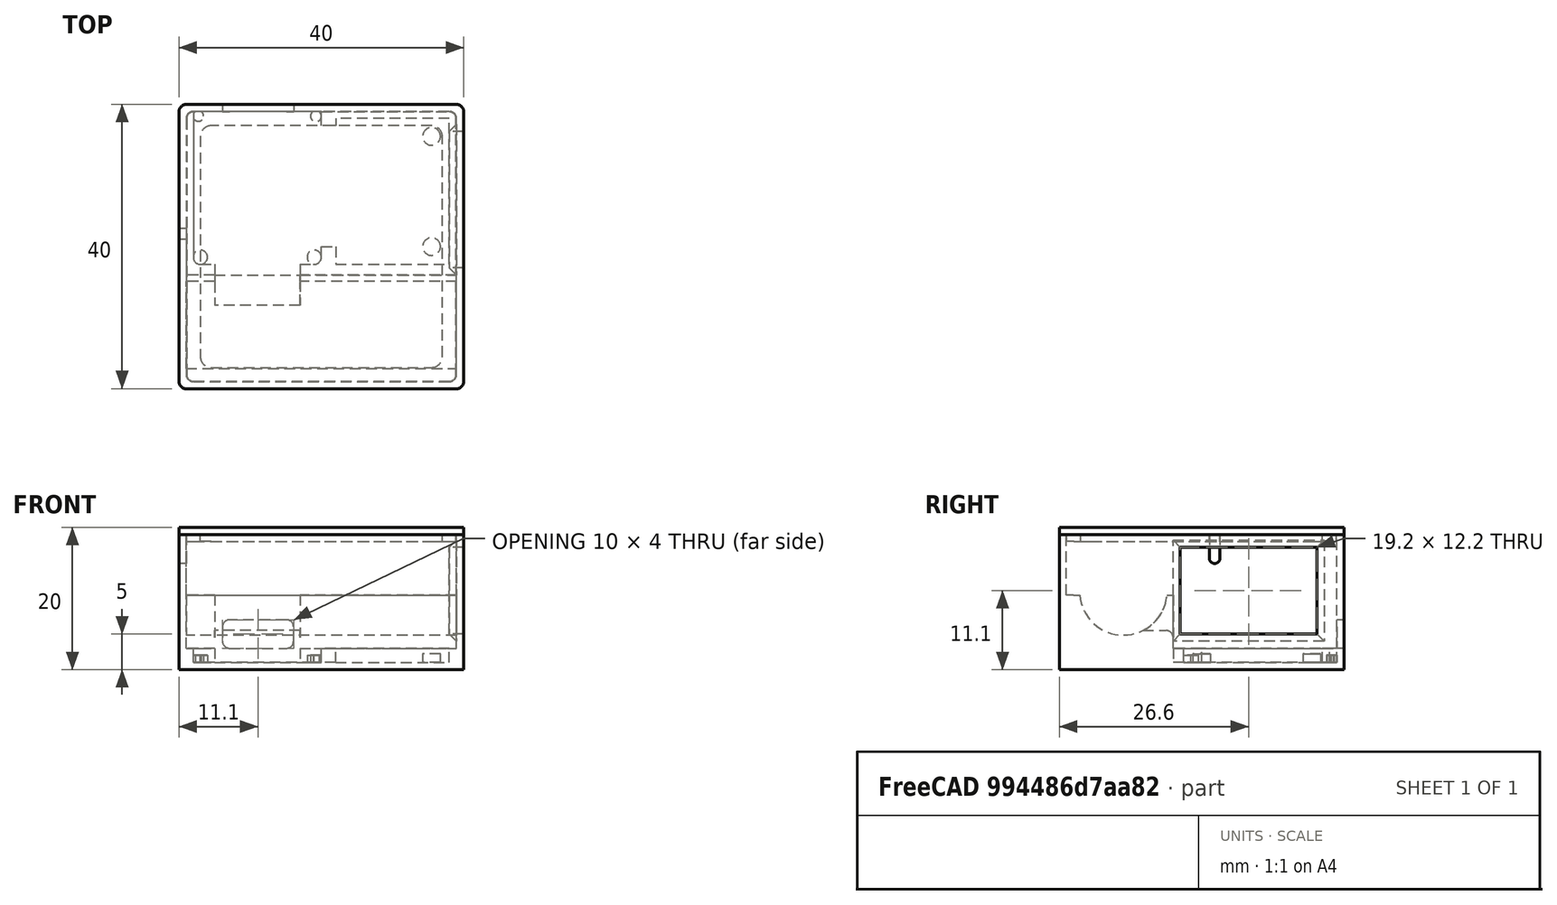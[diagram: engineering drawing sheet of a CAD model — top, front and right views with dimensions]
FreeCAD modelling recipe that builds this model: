
FCSTD DOCUMENT  (FreeCAD 1.0R39319 (Git))
Label: box
License: All rights reserved
LicenseURL: https://en.wikipedia.org/wiki/All_rights_reserved
objects: Sketcher::SketchObject×14, PartDesign::Pad×12, PartDesign::Pocket×6, PartDesign::Chamfer×2, PartDesign::Body×2, Mesh::Feature×2, PartDesign::Plane×1, PartDesign::Fillet×1
note: 94 computed .brp shape members not serialized (recipe doc carries the construction recipe); baked Part::Feature solids carry a one-line shape summary decoded from their .brp

FEATURE [Sketcher::SketchObject] Sketch
  ArcFitTolerance = 1e-06
  AttachmentSupport = -> [XY_Plane]
  FullyConstrained = true
  MakeInternals = false
  MapMode = 5
  sketch-geometry (12):
    g0: LineSegment StartX=1 StartY=0 StartZ=0 EndX=39 EndY=0 EndZ=0
    g1: LineSegment StartX=40 StartY=1 StartZ=0 EndX=40 EndY=39 EndZ=0
    g2: LineSegment StartX=39 StartY=40 StartZ=0 EndX=1 EndY=40 EndZ=0
    g3: LineSegment StartX=0 StartY=39 StartZ=0 EndX=0 EndY=1 EndZ=0
    g4: ArcOfCircle CenterX=1 CenterY=39 CenterZ=0 NormalX=0 NormalY=0 NormalZ=1 AngleXU=0 Radius=1 StartAngle=1.5708 EndAngle=3.14159
    g5: GeomPoint [constr] X=0 Y=40 Z=0
    g6: ArcOfCircle CenterX=1 CenterY=1 CenterZ=0 NormalX=0 NormalY=0 NormalZ=1 AngleXU=0 Radius=1 StartAngle=3.14159 EndAngle=4.71239
    g7: GeomPoint [constr] X=0 Y=0 Z=0
    g8: ArcOfCircle CenterX=39 CenterY=1 CenterZ=0 NormalX=0 NormalY=0 NormalZ=1 AngleXU=0 Radius=1 StartAngle=4.71239 EndAngle=6.28319
    g9: GeomPoint [constr] X=40 Y=0 Z=0
    g10: ArcOfCircle CenterX=39 CenterY=39 CenterZ=0 NormalX=0 NormalY=0 NormalZ=1 AngleXU=0 Radius=1 StartAngle=-2.7e-15 EndAngle=1.5708
    g11: GeomPoint [constr] X=40 Y=40 Z=0
  constraints (27):
    c: Horizontal(g0)
    c: Horizontal(g2)
    c: Vertical(g1)
    c: Vertical(g3)
    c: Distance(g9,g7) = 40
    c: Distance(g7,g5) = 40
    c: Coincident(g7,g-1)
    c: PointOnObject(g5,g3)
    c: PointOnObject(g5,g2)
    c: Tangent(g3,g4) = -1.5708
    c: Tangent(g2,g4) = -1.5708
    c: PointOnObject(g7,g0)
    c: PointOnObject(g7,g3)
    c: Tangent(g0,g6) = -1.5708
    c: Tangent(g3,g6) = -1.5708
    c: PointOnObject(g9,g0)
    c: PointOnObject(g9,g1)
    c: Tangent(g0,g8) = -1.5708
    c: Tangent(g1,g8) = -1.5708
    c: PointOnObject(g11,g2)
    c: PointOnObject(g11,g1)
    c: Tangent(g2,g10) = -1.5708
    c: Tangent(g1,g10) = -1.5708
    c: Radius(g10) = 1
    c: Radius(g4) = 1
    c: Radius(g6) = 1
    c: Radius(g8) = 1
FEATURE [PartDesign::Pad] Pad
  Direction = (0,0,1)
  Length = 1
  Length2 = 10
  Profile = -> Sketch
  ReferenceAxis = -> Sketch [N_Axis]
  Refine = true
  Suppressed = false
  Type = 0
FEATURE [Sketcher::SketchObject] Sketch001
  ArcFitTolerance = 1e-06
  AttachmentSupport = -> [Pad]
  FullyConstrained = true
  MakeInternals = false
  MapMode = 5
  Placement = pos=(0,0,1) rot=(0,0,1;0rad)
  sketch-geometry (24):
    g0: LineSegment StartX=1 StartY=0 StartZ=0 EndX=39 EndY=0 EndZ=0
    g1: LineSegment StartX=40 StartY=1 StartZ=0 EndX=40 EndY=39 EndZ=0
    g2: LineSegment StartX=39 StartY=40 StartZ=0 EndX=1 EndY=40 EndZ=0
    g3: LineSegment StartX=0 StartY=39 StartZ=0 EndX=0 EndY=1 EndZ=0
    g4: ArcOfCircle CenterX=1 CenterY=39 CenterZ=0 NormalX=0 NormalY=0 NormalZ=1 AngleXU=0 Radius=1 StartAngle=1.5708 EndAngle=3.14159
    g5: GeomPoint [constr] X=0 Y=40 Z=0
    g6: ArcOfCircle CenterX=1 CenterY=1 CenterZ=0 NormalX=0 NormalY=0 NormalZ=1 AngleXU=0 Radius=1 StartAngle=3.14159 EndAngle=4.71239
    g7: GeomPoint [constr] X=0 Y=0 Z=0
    g8: ArcOfCircle CenterX=39 CenterY=1 CenterZ=0 NormalX=0 NormalY=0 NormalZ=1 AngleXU=0 Radius=1 StartAngle=4.71239 EndAngle=6.28319
    g9: GeomPoint [constr] X=40 Y=0 Z=0
    g10: ArcOfCircle CenterX=39 CenterY=39 CenterZ=0 NormalX=0 NormalY=0 NormalZ=1 AngleXU=0 Radius=1 StartAngle=-1.8e-15 EndAngle=1.5708
    g11: GeomPoint [constr] X=40 Y=40 Z=0
    g12: LineSegment StartX=2 StartY=1 StartZ=0 EndX=38 EndY=1 EndZ=0
    g13: LineSegment StartX=39 StartY=2 StartZ=0 EndX=39 EndY=38 EndZ=0
    g14: LineSegment StartX=38 StartY=39 StartZ=0 EndX=2 EndY=39 EndZ=0
    g15: LineSegment StartX=1 StartY=38 StartZ=0 EndX=1 EndY=2 EndZ=0
    g16: ArcOfCircle CenterX=2 CenterY=38 CenterZ=0 NormalX=0 NormalY=0 NormalZ=1 AngleXU=0 Radius=1 StartAngle=1.5708 EndAngle=3.14159
    g17: GeomPoint [constr] X=1 Y=39 Z=0
    g18: ArcOfCircle CenterX=38 CenterY=38 CenterZ=0 NormalX=0 NormalY=0 NormalZ=1 AngleXU=0 Radius=1 StartAngle=1.6e-15 EndAngle=1.5708
    g19: GeomPoint [constr] X=39 Y=39 Z=0
    g20: ArcOfCircle CenterX=38 CenterY=2 CenterZ=0 NormalX=0 NormalY=0 NormalZ=1 AngleXU=0 Radius=1 StartAngle=4.71239 EndAngle=6.28319
    g21: GeomPoint [constr] X=39 Y=1 Z=0
    g22: ArcOfCircle CenterX=2 CenterY=2 CenterZ=0 NormalX=0 NormalY=0 NormalZ=1 AngleXU=0 Radius=1 StartAngle=3.14159 EndAngle=4.71239
    g23: GeomPoint [constr] X=1 Y=1 Z=0
  constraints (53):
    c: Horizontal(g0)
    c: Horizontal(g2)
    c: Vertical(g1)
    c: Vertical(g3)
    c: Distance(g9,g7) = 40
    c: Distance(g7,g5) = 40
    c: Coincident(g7,g-1)
    c: PointOnObject(g5,g3)
    c: PointOnObject(g5,g2)
    c: Tangent(g3,g4) = -1.5708
    c: Tangent(g2,g4) = -1.5708
    c: PointOnObject(g7,g0)
    c: PointOnObject(g7,g3)
    c: Tangent(g0,g6) = -1.5708
    c: Tangent(g3,g6) = -1.5708
    c: PointOnObject(g9,g0)
    c: PointOnObject(g9,g1)
    c: Tangent(g0,g8) = -1.5708
    c: Tangent(g1,g8) = -1.5708
    c: PointOnObject(g11,g2)
    c: PointOnObject(g11,g1)
    c: Tangent(g2,g10) = -1.5708
    c: Tangent(g1,g10) = -1.5708
    c: Radius(g10) = 1
    c: Radius(g4) = 1
    c: Radius(g6) = 1
    c: Radius(g8) = 1
    c: Horizontal(g12)
    c: Horizontal(g14)
    c: Vertical(g13)
    c: Vertical(g15)
    c: Coincident(g23,g6)
    c: Coincident(g19,g10)
    c: PointOnObject(g17,g15)
    c: PointOnObject(g17,g14)
    c: Tangent(g15,g16) = -1.5708
    c: Tangent(g14,g16) = -1.5708
    c: PointOnObject(g19,g13)
    c: PointOnObject(g19,g14)
    c: Tangent(g13,g18) = -1.5708
    c: Tangent(g14,g18) = -1.5708
    c: PointOnObject(g21,g13)
    c: PointOnObject(g21,g12)
    c: Tangent(g13,g20) = -1.5708
    c: Tangent(g12,g20) = -1.5708
    c: PointOnObject(g23,g12)
    c: PointOnObject(g23,g15)
    c: Tangent(g12,g22) = -1.5708
    c: Tangent(g15,g22) = -1.5708
    c: Radius(g22) = 1
    c: Radius(g20) = 1
    c: Radius(g18) = 1
    c: Radius(g16) = 1
FEATURE [PartDesign::Pad] Pad001
  BaseFeature = -> Pad
  Direction = (0,0,1)
  Length = 18
  Length2 = 10
  Profile = -> Sketch001
  ReferenceAxis = -> Sketch001 [N_Axis]
  Refine = true
  Suppressed = false
  Type = 0
FEATURE [Sketcher::SketchObject] Sketch002
  ArcFitTolerance = 1e-06
  AttachmentSupport = -> [Pad001]
  FullyConstrained = true
  MakeInternals = false
  MapMode = 5
  Placement = pos=(40,0,0) rot=(0.57735,0.57735,0.57735;2.0944rad)
  sketch-geometry (4):
    g0: LineSegment StartX=36.2 StartY=17.2 StartZ=0 EndX=17 EndY=17.2 EndZ=0
    g1: LineSegment StartX=17 StartY=17.2 StartZ=0 EndX=17 EndY=5 EndZ=0
    g2: LineSegment StartX=17 StartY=5 StartZ=0 EndX=36.2 EndY=5 EndZ=0
    g3: LineSegment StartX=36.2 StartY=5 StartZ=0 EndX=36.2 EndY=17.2 EndZ=0
  constraints (12):
    c: Coincident(g0,g1)
    c: Coincident(g1,g2)
    c: Coincident(g2,g3)
    c: Coincident(g3,g0)
    c: Horizontal(g0)
    c: Horizontal(g2)
    c: Vertical(g1)
    c: Vertical(g3)
    c: Distance(g1,g3) = 19.2
    c: Distance(g0,g2) = 12.2
    c: DistanceY(g-1,g2) = 5
    c: DistanceX(g-1,g0) = 17
FEATURE [PartDesign::Pocket] Pocket
  BaseFeature = -> Pad001
  Direction = (-1,0,0)
  Length = 5
  Length2 = 5
  Profile = -> Sketch002
  ReferenceAxis = -> Sketch002 [N_Axis]
  Refine = true
  Suppressed = false
  Type = 0
FEATURE [Sketcher::SketchObject] Sketch003
  ArcFitTolerance = 1e-06
  AttachmentSupport = -> [Pocket]
  ExternalGeometry = -> [Pocket]
  FullyConstrained = true
  MakeInternals = false
  MapMode = 5
  Placement = pos=(39,0,0) rot=(0.57735,-0.57735,-0.57735;2.0944rad)
  sketch-geometry (8):
    g0: LineSegment StartX=-36.2 StartY=17.2 StartZ=0 EndX=-36.2 EndY=5 EndZ=0
    g1: LineSegment StartX=-36.2 StartY=5 StartZ=0 EndX=-17 EndY=5 EndZ=0
    g2: LineSegment StartX=-17 StartY=5 StartZ=0 EndX=-17 EndY=17.2 EndZ=0
    g3: LineSegment StartX=-17 StartY=17.2 StartZ=0 EndX=-36.2 EndY=17.2 EndZ=0
    g4: LineSegment StartX=-37.2 StartY=18.2 StartZ=0 EndX=-37.2 EndY=4 EndZ=0
    g5: LineSegment StartX=-37.2 StartY=4 StartZ=0 EndX=-16 EndY=4 EndZ=0
    g6: LineSegment StartX=-16 StartY=4 StartZ=0 EndX=-16 EndY=18.2 EndZ=0
    g7: LineSegment StartX=-16 StartY=18.2 StartZ=0 EndX=-37.2 EndY=18.2 EndZ=0
  constraints (22):
    c: Coincident(g0,g1)
    c: Coincident(g1,g2)
    c: Coincident(g2,g3)
    c: Coincident(g3,g0)
    c: Vertical(g0)
    c: Vertical(g2)
    c: Horizontal(g1)
    c: Horizontal(g3)
    c: Coincident(g0,g-3)
    c: Coincident(g1,g-4)
    c: Coincident(g4,g5)
    c: Coincident(g5,g6)
    c: Coincident(g6,g7)
    c: Coincident(g7,g4)
    c: Vertical(g4)
    c: Vertical(g6)
    c: Horizontal(g5)
    c: Horizontal(g7)
    c: DistanceY(g2,g6) = 1
    c: DistanceY(g5,g1) = 1
    c: DistanceX(g1,g5) = 1
    c: DistanceX(g4,g0) = 1
FEATURE [PartDesign::Pad] Pad002
  BaseFeature = -> Pocket
  Direction = (-1,0,0)
  Length = 1
  Length2 = 10
  Profile = -> Sketch003
  ReferenceAxis = -> Sketch003 [N_Axis]
  Refine = true
  Suppressed = false
  Type = 0
FEATURE [PartDesign::Chamfer] Chamfer
  Angle = 45
  Base = -> Pad002 [Edge64,Edge63,Edge61,Edge59]
  BaseFeature = -> Pad002
  ChamferType = 0
  FlipDirection = false
  Refine = true
  Size = 0.99
  Size2 = 1
  SupportTransform = false
  Suppressed = false
  UseAllEdges = false
FEATURE [Sketcher::SketchObject] Sketch004
  ArcFitTolerance = 1e-06
  AttachmentSupport = -> [Chamfer]
  FullyConstrained = false
  MakeInternals = false
  MapMode = 5
  Placement = pos=(0,0,1) rot=(0,0,1;0rad)
  sketch-geometry (24):
    g0: LineSegment StartX=2 StartY=39 StartZ=0 EndX=2 EndY=18.5 EndZ=0
    g1: LineSegment StartX=3 StartY=17.5 StartZ=0 EndX=5 EndY=17.5 EndZ=0
    g2: LineSegment StartX=20 StartY=18.5 StartZ=0 EndX=20 EndY=20 EndZ=0
    g3: ArcOfCircle CenterX=3 CenterY=18.5 CenterZ=0 NormalX=0 NormalY=0 NormalZ=1 AngleXU=0 Radius=1 StartAngle=3.14159 EndAngle=4.71239
    g4: GeomPoint [constr] X=2 Y=17.5 Z=0
    g5: ArcOfCircle CenterX=19 CenterY=18.5 CenterZ=0 NormalX=0 NormalY=0 NormalZ=1 AngleXU=0 Radius=1 StartAngle=4.71239 EndAngle=6.28319
    g6: GeomPoint [constr] X=20 Y=17.5 Z=0
    g7: LineSegment StartX=22 StartY=38 StartZ=0 EndX=22 EndY=37 EndZ=0
    g8: LineSegment StartX=22 StartY=17.5 StartZ=0 EndX=38 EndY=17.5 EndZ=0
    g9: LineSegment StartX=38 StartY=17.5 StartZ=0 EndX=38 EndY=38 EndZ=0
    g10: LineSegment StartX=38 StartY=38 StartZ=0 EndX=22 EndY=38 EndZ=0
    g11: LineSegment StartX=20 StartY=20 StartZ=0 EndX=22 EndY=20 EndZ=0
    g12: LineSegment StartX=22 StartY=37 StartZ=0 EndX=20 EndY=37 EndZ=0
    g13: LineSegment StartX=5 StartY=17.5 StartZ=0 EndX=5 EndY=14 EndZ=0
    g14: LineSegment StartX=17 StartY=17.5 StartZ=0 EndX=17 EndY=14 EndZ=0
    g15: LineSegment StartX=5 StartY=14 StartZ=0 EndX=17 EndY=14 EndZ=0
    g16: LineSegment StartX=17 StartY=17.5 StartZ=0 EndX=19 EndY=17.5 EndZ=0
    g17: LineSegment StartX=20 StartY=37 StartZ=0 EndX=20 EndY=39 EndZ=0
    g18: LineSegment StartX=22 StartY=20 StartZ=0 EndX=22 EndY=17.5 EndZ=0
    g19: LineSegment StartX=1 StartY=1 StartZ=0 EndX=39 EndY=1 EndZ=0
    g20: LineSegment StartX=39 StartY=1 StartZ=0 EndX=39 EndY=39 EndZ=0
    g21: LineSegment StartX=1 StartY=39 StartZ=0 EndX=1 EndY=1 EndZ=0
    g22: LineSegment StartX=1 StartY=39 StartZ=0 EndX=2 EndY=39 EndZ=0
    g23: LineSegment StartX=20 StartY=39 StartZ=0 EndX=39 EndY=39 EndZ=0
  constraints (63):
    c: Vertical(g0)
    c: Vertical(g2)
    c: Horizontal(g1)
    c: Distance(g0,g17) = 18
    c: Distance(g4,g0) = 21.5
    c: PointOnObject(g4,g1)
    c: PointOnObject(g4,g0)
    c: Tangent(g1,g3) = -1.5708
    c: Tangent(g0,g3) = -1.5708
    c: PointOnObject(g6,g16)
    c: PointOnObject(g6,g2)
    c: Coincident(g16,g5) = -1.5708
    c: Tangent(g2,g5) = -1.5708
    c: Coincident(g18,g8)
    c: Coincident(g8,g9)
    c: Coincident(g9,g10)
    c: Coincident(g10,g7)
    c: Vertical(g7)
    c: Vertical(g9)
    c: Horizontal(g8)
    c: Horizontal(g10)
    c: DistanceX(g10,g10) = 16
    c: DistanceY(g9,g9) = 20.5
    c: DistanceX(g-1,g9) = 38
    c: DistanceY(g-1,g7) = 38
    c: PointOnObject(g11,g18)
    c: Horizontal(g11)
    c: PointOnObject(g12,g17)
    c: Horizontal(g12)
    c: DistanceY(g-1,g11) = 20
    c: DistanceY(g-1,g12) = 37
    c: Radius(g3) = 1
    c: Radius(g5) = 1
    c: Vertical(g13)
    c: PointOnObject(g14,g16)
    c: Vertical(g14)
    c: Coincident(g15,g13)
    c: Coincident(g15,g14)
    c: Horizontal(g15)
    c: DistanceY(g13,g13) = 3.5
    c: DistanceX(g-1,g13) = 5
    c: DistanceX(g-1,g14) = 17
    c: Coincident(g1,g13)
    c: PointOnObject(g16,g14)
    c: Coincident(g2,g11)
    c: PointOnObject(g17,g12)
    c: Coincident(g7,g12)
    c: PointOnObject(g18,g11)
    c: Coincident(g19,g20)
    c: Coincident(g21,g19)
    c: Horizontal(g19)
    c: Vertical(g20)
    c: Vertical(g21)
    c: Distance(g20,g21) = 38
    c: Distance(g19,g21) = 38
    c: DistanceX(g-1,g19) = 1
    c: DistanceY(g-1,g19) = 1
    c: Coincident(g22,g21)
    c: Coincident(g22,g0)
    c: Horizontal(g22)
    c: Coincident(g23,g17)
    c: Coincident(g23,g20)
    c: Horizontal(g23)
FEATURE [PartDesign::Pad] Pad003
  BaseFeature = -> Chamfer
  Direction = (0,0,1)
  Length = 2
  Length2 = 10
  Profile = -> Sketch004
  ReferenceAxis = -> Sketch004 [N_Axis]
  Refine = true
  Suppressed = false
  Type = 0
FEATURE [PartDesign::Chamfer] Chamfer001
  Angle = 45
  Base = -> Pad003 [Edge33]
  BaseFeature = -> Pad003
  ChamferType = 0
  FlipDirection = false
  Refine = true
  Size = 1.8
  Size2 = 1
  SupportTransform = false
  Suppressed = false
  UseAllEdges = false
FEATURE [Sketcher::SketchObject] Sketch005
  ArcFitTolerance = 1e-06
  AttachmentSupport = -> [Chamfer001]
  ExternalGeometry = -> [Chamfer001]
  FullyConstrained = true
  MakeInternals = false
  MapMode = 5
  Placement = pos=(0,0,3) rot=(0,0,1;0rad)
  sketch-geometry (4):
    g0: LineSegment StartX=2 StartY=1 StartZ=0 EndX=38 EndY=1 EndZ=0
    g1: LineSegment StartX=38 StartY=1 StartZ=0 EndX=38 EndY=16 EndZ=0
    g2: LineSegment StartX=38 StartY=16 StartZ=0 EndX=2 EndY=16 EndZ=0
    g3: LineSegment StartX=2 StartY=16 StartZ=0 EndX=2 EndY=1 EndZ=0
  constraints (11):
    c: Coincident(g0,g1)
    c: Coincident(g1,g2)
    c: Coincident(g2,g3)
    c: Coincident(g3,g0)
    c: Horizontal(g0)
    c: Horizontal(g2)
    c: Vertical(g1)
    c: Vertical(g3)
    c: Distance(g1,g3) = 36
    c: Distance(g0,g2) = 15
    c: Coincident(g0,g-3)
FEATURE [PartDesign::Pad] Pad004
  BaseFeature = -> Chamfer001
  Direction = (0,0,1)
  Length = 5
  Length2 = 10
  Midplane = true
  Profile = -> Sketch005
  ReferenceAxis = -> Sketch005 [N_Axis]
  Refine = true
  Suppressed = false
  Type = 0
FEATURE [PartDesign::Pad] Pad005
  BaseFeature = -> Pad004
  Direction = (0,0,1)
  Length = 10
  Length2 = 10
  Profile = -> Pad004 [Face29]
  Refine = true
  Suppressed = false
  Type = 0
FEATURE [Sketcher::SketchObject] Sketch006
  ArcFitTolerance = 1e-06
  AttachmentSupport = -> [Pad005]
  ExternalGeometry = -> [Pad005]
  FullyConstrained = false
  MakeInternals = false
  MapMode = 5
  Placement = pos=(0,0,1) rot=(0,0,1;0rad)
  sketch-geometry (4):
    g0: Circle CenterX=3 CenterY=18.5 CenterZ=0 NormalX=0 NormalY=0 NormalZ=1 AngleXU=0 Radius=1
    g1: Circle CenterX=19 CenterY=18.5 CenterZ=0 NormalX=0 NormalY=0 NormalZ=1 AngleXU=0 Radius=1
    g2: Circle CenterX=2.69921 CenterY=38.3735 CenterZ=0 NormalX=0 NormalY=0 NormalZ=1 AngleXU=0 Radius=0.751416
    g3: Circle CenterX=19.2468 CenterY=38.3457 CenterZ=0 NormalX=0 NormalY=0 NormalZ=1 AngleXU=0 Radius=0.769216
  constraints (4):
    c: Coincident(g0,g-3)
    c: PointOnObject(g-3,g0)
    c: Coincident(g1,g-4)
    c: PointOnObject(g-4,g1)
FEATURE [PartDesign::Pad] Pad006
  BaseFeature = -> Pad005
  Direction = (0,0,1)
  Length = 1
  Length2 = 10
  Profile = -> Sketch006
  ReferenceAxis = -> Sketch006 [N_Axis]
  Refine = true
  Suppressed = false
  Type = 0
FEATURE [Sketcher::SketchObject] Sketch007
  ArcFitTolerance = 1e-06
  AttachmentSupport = -> [Pad006]
  ExternalGeometry = -> [Pad006]
  FullyConstrained = true
  MakeInternals = false
  MapMode = 5
  Placement = pos=(0,0,1) rot=(0,0,1;0rad)
  sketch-geometry (2):
    g0: Circle CenterX=35.5 CenterY=35.5 CenterZ=0 NormalX=0 NormalY=0 NormalZ=1 AngleXU=0 Radius=1.25
    g1: Circle CenterX=35.5 CenterY=20 CenterZ=0 NormalX=0 NormalY=0 NormalZ=1 AngleXU=0 Radius=1.25
  constraints (6):
    c: Diameter(g0) = 2.5
    c: Diameter(g1) = 2.5
    c: DistanceX(g1,g-3) = 2.5
    c: DistanceX(g0,g-3) = 2.5
    c: DistanceY(g0,g-3) = 2.5
    c: DistanceY(g-4,g1) = 2.5
FEATURE [PartDesign::Pad] Pad007
  BaseFeature = -> Pad006
  Direction = (0,0,1)
  Length = 1.2
  Length2 = 10
  Profile = -> Sketch007
  ReferenceAxis = -> Sketch007 [N_Axis]
  Refine = true
  Suppressed = false
  Type = 0
FEATURE [PartDesign::Plane] DatumPlane
  AttachmentOffset = pos=(0,0,20) rot=(0,0,1;0rad)
  AttachmentSupport = -> [YZ_Plane]
  Length = 76.4018
  MapMode = 5
  Placement = pos=(20,0,0) rot=(0.57735,0.57735,0.57735;2.0944rad)
  ResizeMode = 0
  Width = 61.4018
FEATURE [Sketcher::SketchObject] Sketch008
  ArcFitTolerance = 1e-06
  AttachmentSupport = -> [DatumPlane]
  FullyConstrained = true
  MakeInternals = false
  MapMode = 5
  Placement = pos=(20,0,0) rot=(0.57735,0.57735,0.57735;2.0944rad)
  sketch-geometry (1):
    g0: Circle CenterX=9 CenterY=11 CenterZ=0 NormalX=0 NormalY=0 NormalZ=1 AngleXU=0 Radius=6.15
  constraints (3):
    c: Diameter(g0) = 12.3
    c: DistanceY(g-1,g0) = 11
    c: DistanceX(g-1,g0) = 9
FEATURE [PartDesign::Pocket] Pocket001
  BaseFeature = -> Pad007
  Direction = (0,0,-1)
  Length = 5
  Length2 = 5
  Profile = -> Pad007 [Face39]
  Refine = true
  Suppressed = false
  Type = 0
FEATURE [PartDesign::Pocket] Pocket002
  BaseFeature = -> Pocket001
  Direction = (-1,0,0)
  Length = 38
  Length2 = 5
  Midplane = true
  Profile = -> Sketch008
  ReferenceAxis = -> Sketch008 [N_Axis]
  Refine = true
  Suppressed = false
  Type = 0
FEATURE [PartDesign::Pad] Pad008
  BaseFeature = -> Pocket002
  Direction = (-1,0,0)
  Length = 1
  Length2 = 10
  Profile = -> Pocket002 [Face46]
  Refine = true
  Suppressed = false
  Type = 0
FEATURE [PartDesign::Pad] Pad009
  BaseFeature = -> Pad008
  Direction = (1,0,0)
  Length = 1
  Length2 = 10
  Profile = -> Pad008 [Face32]
  Refine = true
  Suppressed = false
  Type = 0
FEATURE [Sketcher::SketchObject] Sketch009
  ArcFitTolerance = 1e-06
  AttachmentSupport = -> [Pad009]
  ExternalGeometry = -> [Pad009]
  FullyConstrained = true
  MakeInternals = false
  MapMode = 5
  Placement = pos=(0,0,10.5) rot=(0,0,1;0rad)
  sketch-geometry (4):
    g0: LineSegment StartX=5 StartY=16 StartZ=0 EndX=5 EndY=11 EndZ=0
    g1: LineSegment StartX=5 StartY=11 StartZ=0 EndX=17 EndY=11 EndZ=0
    g2: LineSegment StartX=17 StartY=11 StartZ=0 EndX=17 EndY=16 EndZ=0
    g3: LineSegment StartX=17 StartY=16 StartZ=0 EndX=5 EndY=16 EndZ=0
  constraints (12):
    c: Coincident(g0,g1)
    c: Coincident(g1,g2)
    c: Coincident(g2,g3)
    c: Coincident(g3,g0)
    c: Vertical(g0)
    c: Vertical(g2)
    c: Horizontal(g1)
    c: Horizontal(g3)
    c: Distance(g0,g2) = 12
    c: Distance(g1,g3) = 5
    c: PointOnObject(g0,g-3)
    c: DistanceX(g-1,g0) = 5
FEATURE [PartDesign::Pocket] Pocket003
  BaseFeature = -> Pad009
  Direction = (0,0,-1)
  Length = 5
  Length2 = 5
  Profile = -> Sketch009
  ReferenceAxis = -> Sketch009 [N_Axis]
  Refine = true
  Suppressed = false
  Type = 0
FEATURE [PartDesign::Fillet] Fillet
  Base = -> Pocket003 [Edge81]
  BaseFeature = -> Pocket003
  Radius = 1
  Refine = true
  SupportTransform = false
  Suppressed = false
  UseAllEdges = false
FEATURE [Sketcher::SketchObject] Sketch010
  ArcFitTolerance = 1e-06
  AttachmentSupport = -> [Fillet]
  FullyConstrained = false
  MakeInternals = false
  MapMode = 5
  Placement = pos=(0,0,0) rot=(0.57735,-0.57735,-0.57735;2.0944rad)
  sketch-geometry (4):
    g0: ArcOfCircle CenterX=-21.8272 CenterY=15.6733 CenterZ=0 NormalX=0 NormalY=0 NormalZ=1 AngleXU=0 Radius=0.75 StartAngle=3.14159 EndAngle=6.28319
    g1: ArcOfCircle CenterX=-21.8272 CenterY=20.6733 CenterZ=0 NormalX=0 NormalY=0 NormalZ=1 AngleXU=0 Radius=0.75 StartAngle=0 EndAngle=3.14159
    g2: LineSegment StartX=-22.5772 StartY=15.6733 StartZ=0 EndX=-22.5772 EndY=20.6733 EndZ=0
    g3: LineSegment StartX=-21.0772 StartY=15.6733 StartZ=0 EndX=-21.0772 EndY=20.6733 EndZ=0
  constraints (8):
    c: Tangent(g0,g2) = 1.5708
    c: Tangent(g0,g3) = -1.5708
    c: Tangent(g1,g2) = 1.5708
    c: Tangent(g1,g3) = -1.5708
    c: Equal(g0,g1)
    c: Vertical(g3)
    c: Distance(g0,g1) = 5
    c: Radius(g0) = 0.75
FEATURE [PartDesign::Pocket] Pocket004
  BaseFeature = -> Fillet
  Direction = (1,0,0)
  Length = 5
  Length2 = 5
  Profile = -> Sketch010
  ReferenceAxis = -> Sketch010 [N_Axis]
  Refine = true
  Suppressed = false
  Type = 0
FEATURE [Sketcher::SketchObject] Sketch011
  ArcFitTolerance = 1e-06
  AttachmentSupport = -> [XY_Plane001]
  FullyConstrained = true
  MakeInternals = false
  MapMode = 5
  sketch-geometry (24):
    g0: LineSegment StartX=2.05 StartY=1.05 StartZ=0 EndX=37.95 EndY=1.05 EndZ=0
    g1: LineSegment StartX=38.95 StartY=2.05 StartZ=0 EndX=38.95 EndY=37.95 EndZ=0
    g2: LineSegment StartX=37.95 StartY=38.95 StartZ=0 EndX=2.05 EndY=38.95 EndZ=0
    g3: LineSegment StartX=1.05 StartY=37.95 StartZ=0 EndX=1.05 EndY=2.05 EndZ=0
    g4: ArcOfCircle CenterX=2.05 CenterY=2.05 CenterZ=0 NormalX=0 NormalY=0 NormalZ=1 AngleXU=0 Radius=1 StartAngle=3.14159 EndAngle=4.71239
    g5: GeomPoint [constr] X=1.05 Y=1.05 Z=0
    g6: ArcOfCircle CenterX=37.95 CenterY=2.05 CenterZ=0 NormalX=0 NormalY=0 NormalZ=1 AngleXU=0 Radius=1 StartAngle=4.71239 EndAngle=6.28319
    g7: GeomPoint [constr] X=38.95 Y=1.05 Z=0
    g8: ArcOfCircle CenterX=2.05 CenterY=37.95 CenterZ=0 NormalX=0 NormalY=0 NormalZ=1 AngleXU=0 Radius=1 StartAngle=1.5708 EndAngle=3.14159
    g9: GeomPoint [constr] X=1.05 Y=38.95 Z=0
    g10: ArcOfCircle CenterX=37.95 CenterY=37.95 CenterZ=0 NormalX=0 NormalY=0 NormalZ=1 AngleXU=0 Radius=1 StartAngle=3.6e-15 EndAngle=1.5708
    g11: GeomPoint [constr] X=38.95 Y=38.95 Z=0
    g12: LineSegment StartX=4.5 StartY=3 StartZ=0 EndX=35.5 EndY=3 EndZ=0
    g13: LineSegment StartX=37 StartY=4.5 StartZ=0 EndX=37 EndY=35.5 EndZ=0
    g14: LineSegment StartX=35.5 StartY=37 StartZ=0 EndX=4.5 EndY=37 EndZ=0
    g15: LineSegment StartX=3 StartY=35.5 StartZ=0 EndX=3 EndY=4.5 EndZ=0
    g16: ArcOfCircle CenterX=4.5 CenterY=35.5 CenterZ=0 NormalX=0 NormalY=0 NormalZ=1 AngleXU=0 Radius=1.5 StartAngle=1.5708 EndAngle=3.14159
    g17: GeomPoint [constr] X=3 Y=37 Z=0
    g18: ArcOfCircle CenterX=35.5 CenterY=35.5 CenterZ=0 NormalX=0 NormalY=0 NormalZ=1 AngleXU=0 Radius=1.5 StartAngle=0 EndAngle=1.5708
    g19: GeomPoint [constr] X=37 Y=37 Z=0
    g20: ArcOfCircle CenterX=35.5 CenterY=4.5 CenterZ=0 NormalX=0 NormalY=0 NormalZ=1 AngleXU=0 Radius=1.5 StartAngle=4.71239 EndAngle=6.28319
    g21: GeomPoint [constr] X=37 Y=3 Z=0
    g22: ArcOfCircle CenterX=4.5 CenterY=4.5 CenterZ=0 NormalX=0 NormalY=0 NormalZ=1 AngleXU=0 Radius=1.5 StartAngle=3.14159 EndAngle=4.71239
    g23: GeomPoint [constr] X=3 Y=3 Z=0
  constraints (56):
    c: Horizontal(g0)
    c: Horizontal(g2)
    c: Vertical(g1)
    c: Vertical(g3)
    c: DistanceX(g9,g11) = 37.9
    c: DistanceY(g5,g9) = 37.9
    c: DistanceY(g-1,g5) = 1.05
    c: DistanceX(g-1,g5) = 1.05
    c: PointOnObject(g5,g0)
    c: PointOnObject(g5,g3)
    c: Tangent(g0,g4) = -1.5708
    c: Tangent(g3,g4) = -1.5708
    c: PointOnObject(g7,g0)
    c: PointOnObject(g7,g1)
    c: Tangent(g0,g6) = -1.5708
    c: Tangent(g1,g6) = -1.5708
    c: PointOnObject(g9,g3)
    c: PointOnObject(g9,g2)
    c: Tangent(g3,g8) = -1.5708
    c: Tangent(g2,g8) = -1.5708
    c: PointOnObject(g11,g2)
    c: PointOnObject(g11,g1)
    c: Tangent(g2,g10) = -1.5708
    c: Tangent(g1,g10) = -1.5708
    c: Radius(g8) = 1
    c: Radius(g10) = 1
    c: Radius(g6) = 1
    c: Radius(g4) = 1
    c: Horizontal(g12)
    c: Horizontal(g14)
    c: Vertical(g13)
    c: Vertical(g15)
    c: DistanceX(g-1,g23) = 3
    c: DistanceY(g-1,g23) = 3
    c: DistanceX(g-1,g21) = 37
    c: DistanceY(g-1,g17) = 37
    c: PointOnObject(g17,g15)
    c: PointOnObject(g17,g14)
    c: Tangent(g15,g16) = -1.5708
    c: Tangent(g14,g16) = -1.5708
    c: PointOnObject(g19,g14)
    c: PointOnObject(g19,g13)
    c: Tangent(g14,g18) = -1.5708
    c: Tangent(g13,g18) = -1.5708
    c: PointOnObject(g21,g12)
    c: PointOnObject(g21,g13)
    c: Tangent(g12,g20) = -1.5708
    c: Tangent(g13,g20) = -1.5708
    c: PointOnObject(g23,g12)
    c: PointOnObject(g23,g15)
    c: Tangent(g12,g22) = -1.5708
    c: Tangent(g15,g22) = -1.5708
    c: Radius(g22) = 1.5
    c: Radius(g20) = 1.5
    c: Radius(g16) = 1.5
    c: Radius(g18) = 1.5
FEATURE [PartDesign::Pad] Pad010
  Direction = (0,0,1)
  Length = 1
  Length2 = 10
  Profile = -> Sketch011
  ReferenceAxis = -> Sketch011 [N_Axis]
  Refine = true
  Suppressed = false
  Type = 0
FEATURE [Sketcher::SketchObject] Sketch012
  ArcFitTolerance = 1e-06
  AttachmentSupport = -> [Pad010]
  FullyConstrained = true
  MakeInternals = false
  MapMode = 5
  Placement = pos=(0,0,1) rot=(0,0,1;0rad)
  sketch-geometry (12):
    g0: LineSegment StartX=1 StartY=2e-16 StartZ=0 EndX=39 EndY=2e-16 EndZ=0
    g1: LineSegment StartX=40 StartY=1 StartZ=0 EndX=40 EndY=39 EndZ=0
    g2: LineSegment StartX=39 StartY=40 StartZ=0 EndX=1 EndY=40 EndZ=0
    g3: LineSegment StartX=0 StartY=39 StartZ=0 EndX=0 EndY=1 EndZ=0
    g4: ArcOfCircle CenterX=1 CenterY=1 CenterZ=0 NormalX=0 NormalY=0 NormalZ=1 AngleXU=0 Radius=1 StartAngle=3.14159 EndAngle=4.71239
    g5: GeomPoint [constr] X=0 Y=0 Z=0
    g6: ArcOfCircle CenterX=39 CenterY=1 CenterZ=0 NormalX=0 NormalY=0 NormalZ=1 AngleXU=0 Radius=1 StartAngle=4.71239 EndAngle=6.28319
    g7: GeomPoint [constr] X=40 Y=0 Z=0
    g8: ArcOfCircle CenterX=1 CenterY=39 CenterZ=0 NormalX=0 NormalY=0 NormalZ=1 AngleXU=0 Radius=1 StartAngle=1.5708 EndAngle=3.14159
    g9: GeomPoint [constr] X=0 Y=40 Z=0
    g10: ArcOfCircle CenterX=39 CenterY=39 CenterZ=0 NormalX=0 NormalY=0 NormalZ=1 AngleXU=0 Radius=1 StartAngle=0 EndAngle=1.5708
    g11: GeomPoint [constr] X=40 Y=40 Z=0
  constraints (27):
    c: Horizontal(g0)
    c: Horizontal(g2)
    c: Vertical(g1)
    c: Vertical(g3)
    c: Distance(g7,g5) = 40
    c: Distance(g5,g9) = 40
    c: Coincident(g5,g-1)
    c: PointOnObject(g5,g0)
    c: PointOnObject(g5,g3)
    c: Tangent(g0,g4) = -1.5708
    c: Tangent(g3,g4) = -1.5708
    c: PointOnObject(g7,g0)
    c: PointOnObject(g7,g1)
    c: Tangent(g0,g6) = -1.5708
    c: Tangent(g1,g6) = -1.5708
    c: PointOnObject(g9,g3)
    c: PointOnObject(g9,g2)
    c: Tangent(g3,g8) = -1.5708
    c: Tangent(g2,g8) = -1.5708
    c: PointOnObject(g11,g1)
    c: PointOnObject(g11,g2)
    c: Tangent(g1,g10) = -1.5708
    c: Tangent(g2,g10) = -1.5708
    c: Radius(g8) = 1
    c: Radius(g10) = 1
    c: Radius(g6) = 1
    c: Radius(g4) = 1
FEATURE [PartDesign::Pad] Pad011
  BaseFeature = -> Pad010
  Direction = (0,0,1)
  Length = 1
  Length2 = 10
  Profile = -> Sketch012
  ReferenceAxis = -> Sketch012 [N_Axis]
  Refine = true
  Suppressed = false
  Type = 0
FEATURE [PartDesign::Body] Body001
  AllowCompound = false
  Group = -> [Sketch011,Pad010,Sketch012,Pad011]
  Origin = -> Origin001
  Placement = pos=(0,0,18) rot=(0,0,1;0rad)
  Tip = -> Pad011
FEATURE [Sketcher::SketchObject] Sketch013
  ArcFitTolerance = 1e-06
  AttachmentSupport = -> [Pocket004]
  ExternalGeometry = -> [Pocket004]
  FullyConstrained = true
  MakeInternals = false
  MapMode = 5
  Placement = pos=(0,40,0) rot=(0,0.707107,0.707107;3.14159rad)
  sketch-geometry (12):
    g0: LineSegment StartX=-6.1 StartY=4 StartZ=0 EndX=-6.1 EndY=6 EndZ=0
    g1: LineSegment StartX=-7.1 StartY=7 StartZ=0 EndX=-15.1 EndY=7 EndZ=0
    g2: LineSegment StartX=-16.1 StartY=6 StartZ=0 EndX=-16.1 EndY=4 EndZ=0
    g3: LineSegment StartX=-15.1 StartY=3 StartZ=0 EndX=-7.1 EndY=3 EndZ=0
    g4: ArcOfCircle CenterX=-7.1 CenterY=4 CenterZ=0 NormalX=0 NormalY=0 NormalZ=1 AngleXU=0 Radius=1 StartAngle=4.71239 EndAngle=6.28319
    g5: GeomPoint [constr] X=-6.1 Y=3 Z=0
    g6: ArcOfCircle CenterX=-7.1 CenterY=6 CenterZ=0 NormalX=0 NormalY=0 NormalZ=1 AngleXU=0 Radius=1 StartAngle=0 EndAngle=1.5708
    g7: GeomPoint [constr] X=-6.1 Y=7 Z=0
    g8: ArcOfCircle CenterX=-15.1 CenterY=6 CenterZ=0 NormalX=0 NormalY=0 NormalZ=1 AngleXU=0 Radius=1 StartAngle=1.5708 EndAngle=3.14159
    g9: GeomPoint [constr] X=-16.1 Y=7 Z=0
    g10: ArcOfCircle CenterX=-15.1 CenterY=4 CenterZ=0 NormalX=0 NormalY=0 NormalZ=1 AngleXU=0 Radius=1 StartAngle=3.14159 EndAngle=4.71239
    g11: GeomPoint [constr] X=-16.1 Y=3 Z=0
  constraints (28):
    c: Vertical(g0)
    c: Vertical(g2)
    c: Horizontal(g1)
    c: Horizontal(g3)
    c: Distance(g5,g11) = 10
    c: Distance(g7,g5) = 4
    c: DistanceY(g-1,g5) = 3
    c: DistanceX(g5,g-3) = 4.1
    c: PointOnObject(g5,g0)
    c: PointOnObject(g5,g3)
    c: Tangent(g0,g4) = -1.5708
    c: Tangent(g3,g4) = -1.5708
    c: PointOnObject(g7,g0)
    c: PointOnObject(g7,g1)
    c: Tangent(g0,g6) = -1.5708
    c: Tangent(g1,g6) = -1.5708
    c: PointOnObject(g9,g1)
    c: PointOnObject(g9,g2)
    c: Tangent(g1,g8) = -1.5708
    c: Tangent(g2,g8) = -1.5708
    c: PointOnObject(g11,g3)
    c: PointOnObject(g11,g2)
    c: Tangent(g3,g10) = -1.5708
    c: Tangent(g2,g10) = -1.5708
    c: Radius(g4) = 1
    c: Radius(g6) = 1
    c: Radius(g8) = 1
    c: Radius(g10) = 1
FEATURE [PartDesign::Pocket] Pocket005
  BaseFeature = -> Pocket004
  Direction = (0,-1,2e-16)
  Length = 5
  Length2 = 5
  Profile = -> Sketch013
  ReferenceAxis = -> Sketch013 [N_Axis]
  Refine = true
  Suppressed = false
  Type = 0
FEATURE [PartDesign::Body] Body
  AllowCompound = false
  Group = -> [Sketch,Pad,Sketch001,Pad001,Sketch002,Pocket,Sketch003,Pad002,Chamfer,Sketch004,Pad003,Chamfer001,Sketch005,Pad004,Pad005,Sketch006,Pad006,Sketch007,Pad007,DatumPlane,Sketch008,Pocket001,Pocket002,Pad008,Pad009,Sketch009,Pocket003,Fillet,Sketch010,Pocket004,Sketch013,Pocket005]
  Origin = -> Origin
  Tip = -> Pocket005
FEATURE [Mesh::Feature] Mesh  label="Box_main"
FEATURE [Mesh::Feature] Mesh001  label="Box_lid"
